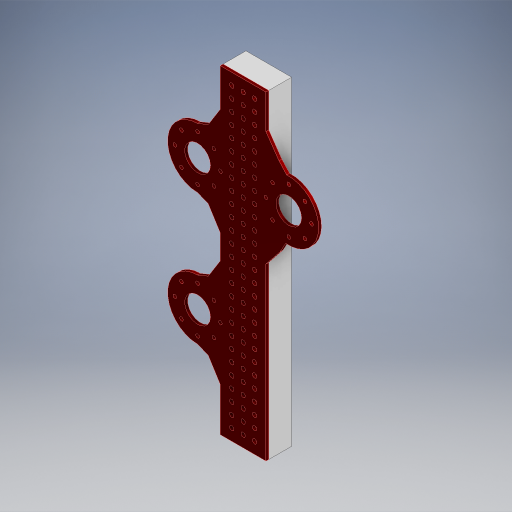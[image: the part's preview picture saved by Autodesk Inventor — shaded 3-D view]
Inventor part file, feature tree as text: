
AUTODESK INVENTOR PART (.ipt)
format: ipt  version: 2024.2 (Build 282272000, 272)  size: 659,968 bytes
history: native  units: in
note: dims shown in document units (in); Inventor stores cm internally (conversion verified against a paired STEP export)
features: extrude x3, sketch x3, projected_geometry x1, other x1
ambient origin geometry x8: Origin, YZ Plane, XZ Plane, XY Plane, X Axis, Y Axis, Z Axis, Center Point
bodies: Solid1 (feature_tree)
feature tree (8):
  extrude  "Extrusion1"  Depth=1.0in
  extrude  "Extrusion2"  Depth=14.0in
  extrude  "Extrusion3"  Depth=0.125in
  sketch  "Sketch1"  dims[d0=2.0in d1=1.0in]
  sketch  "Sketch2"  dims[d2=14.0in d3=0.0in d4=0.196in]
  sketch  "Sketch3"  dims[d5=0.5in d6=0.5in d7=1.1811in d9=0.5in d10=10.6299in d12=0.5in d15=14.0in d16=0.0in d17=1.124in d18=4.0in d19=1.124in d20=4.0in d21=3.991in d22=0.994in d23=1.124in d24=5.75in d25=0.159in d26=0.159in d27=2.0in d28=1.0in d33=1.0in d34=1.5748in d36=360.0deg d38=0.159in d39=1.0in d40=1.5748in d42=360.0deg d44=0.75in d45=0.75in d46=0.75in d47=0.5in d48=1.0in d49=0.5in d50=1.0in d51=0.5in d52=1.0in d53=0.5in d54=1.0in d56=1.0in d57=0.5in d58=1.0in d59=0.125in d60=0.0in d61=3.1496in d63=360.0deg d65=3.1496in d67=360.0deg d73=3.1496in d75=360.0deg]
  projected_geometry  "Projected Loop1"
  other  "2024-210-009-Shooter-Gusset-Plate"
